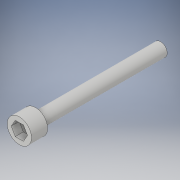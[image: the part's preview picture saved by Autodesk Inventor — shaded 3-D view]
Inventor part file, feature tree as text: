
AUTODESK INVENTOR PART (.ipt)
format: ipt  version: 2018 (Build 220112000, 112)  size: 111,104 bytes
history: native  units: in
note: dims shown in document units (in); Inventor stores cm internally (conversion verified against a paired STEP export)
features: extrude x3, sketch x3
ambient origin geometry x8: Origin, YZ Plane, XZ Plane, XY Plane, X Axis, Y Axis, Z Axis, Center Point
bodies: Solid1 (feature_tree)
feature tree (6):
  extrude  "Extrusion1"  Depth=0.2in TaperAngle=0.0deg
  extrude  "Extrusion2"  Depth=0.1in TaperAngle=0.0deg
  extrude  "Extrusion3"  Depth=1.55in TaperAngle=0.0deg
  sketch  "Sketch1"  dims[d0=0.3in d1=0.2in d2=0.0in]
  sketch  "Sketch2"  dims[d3=0.175in d4=0.1in d5=0.0in]
  sketch  "Sketch3"  dims[d6=0.163in d7=1.55in d8=0.0in]
